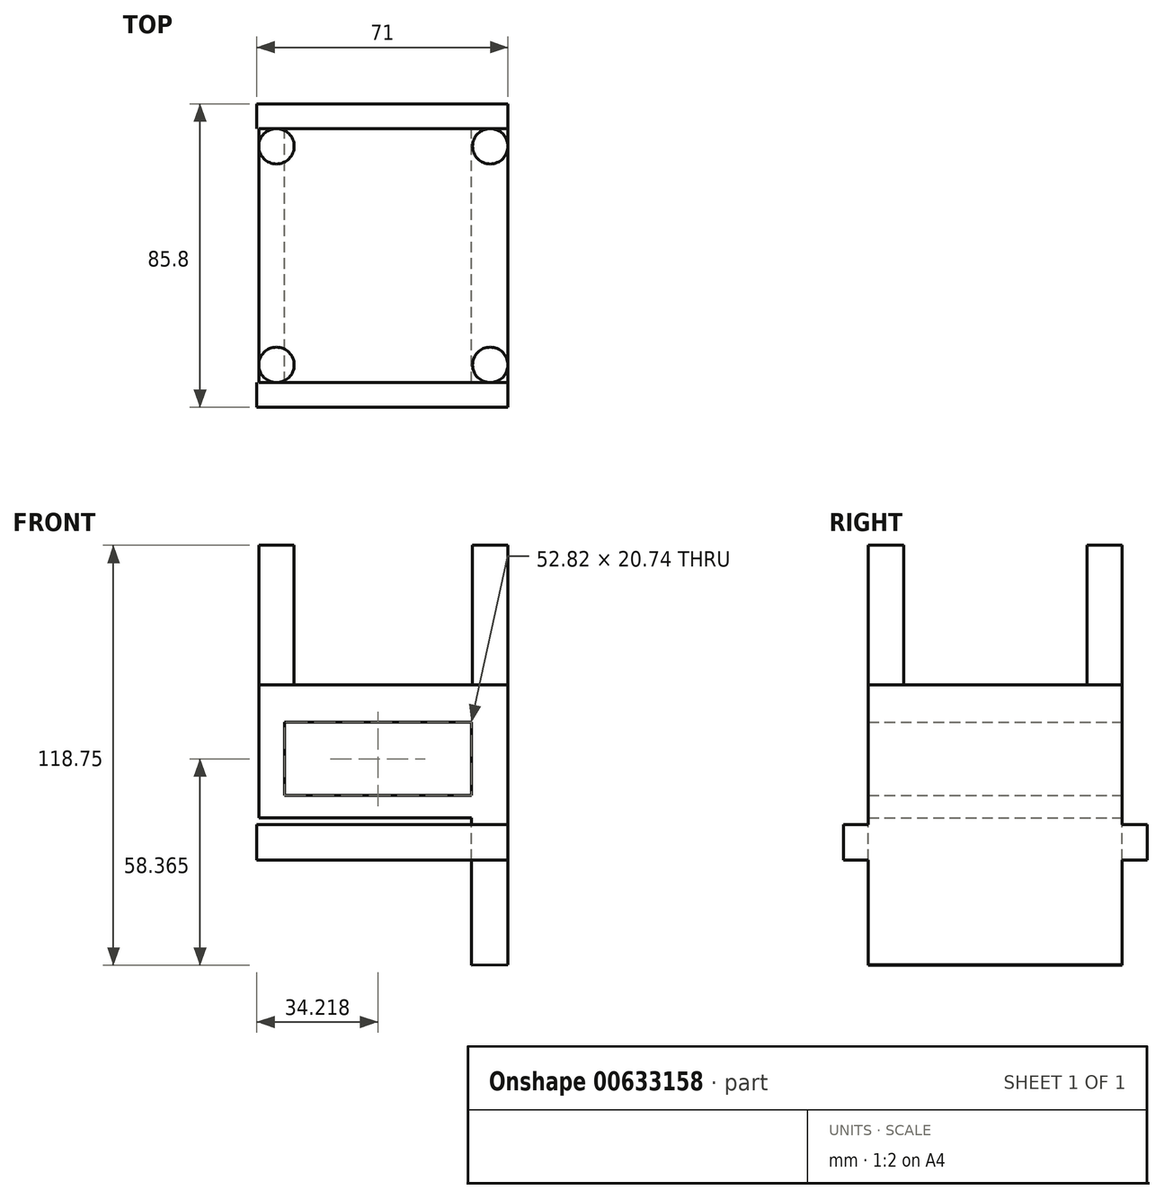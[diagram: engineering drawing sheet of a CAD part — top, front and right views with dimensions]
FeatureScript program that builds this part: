
annotation { "Feature Type Name" : "Feature", "Feature Type Description" : "" }
export const myFeature = defineFeature(function(context is Context, id is Id, definition is map)
    precondition{}
    {
        {
            var Q0;
            Q0=qCreatedBy(makeId("Front.planeOp"),FACE);
            var sketch = newSketch(context, id + "F0", { "sketchPlane" : qUnion([Q0])});
            skLineSegment(sketch, "E0", {"start": v(43.4, -44.81) * mm, "end": v(43.4, 23.93) * mm});
            skLineSegment(sketch, "E1", {"start": v(43.4, 23.93) * mm, "end": v(-16.65, 23.93) * mm});
            skLineSegment(sketch, "E2", {"start": v(-16.65, 23.93) * mm, "end": v(-16.65, 34.54) * mm});
            skLineSegment(sketch, "E3", {"start": v(-16.65, 34.54) * mm, "end": v(53.78, 34.54) * mm});
            skLineSegment(sketch, "E4", {"start": v(53.78, 34.54) * mm, "end": v(53.78, -44.57) * mm});
            skLineSegment(sketch, "E5", {"start": v(53.78, -44.57) * mm, "end": v(43.4, -44.81) * mm});
            skLineSegment(sketch, "E6", {"start": v(43.4, -3.09) * mm, "end": v(-16.65, -3.09) * mm});
            skLineSegment(sketch, "E7", {"start": v(-16.65, -3.09) * mm, "end": v(-16.65, 23.93) * mm});
            skLineSegment(sketch, "E8", {"start": v(43.4, 3.18) * mm, "end": v(-9.41, 3.18) * mm});
            skLineSegment(sketch, "E9", {"start": v(-9.41, 3.18) * mm, "end": v(-9.41, 23.93) * mm});
            skSolve(sketch);
        }
        {
            var Q0;
            Q0 = qSketchRegion(id + "F0", true);
            extrude(context, id + "F1", {"entities" : qUnion([Q0]), "depth" : 71.8 * mm, "offsetDistance" : 25 * mm});
        }
        {
            var Q0;
            Q0=makeQuery(id+"F1.opExtrude","SWEPT_FACE",FACE,{"disambiguationData":[OSD([sQuery(id+"F0.wireOp",EDGE,"E3")])]});
            var sketch = newSketch(context, id + "F2", { "sketchPlane" : qUnion([Q0])});
            skLineSegment(sketch, "E10", {"start": v(-16.65, -71.8) * mm, "end": v(-16.65, -66.8) * mm});
            skLineSegment(sketch, "E11", {"start": v(-11.65, -66.8) * mm, "end": v(-16.65, -66.8) * mm});
            skLineSegment(sketch, "E12", {"start": v(-16.65, 0) * mm, "end": v(-16.65, -5) * mm});
            skLineSegment(sketch, "E13", {"start": v(-16.65, -5) * mm, "end": v(-11.65, -5) * mm});
            skLineSegment(sketch, "E14", {"start": v(53.78, 0) * mm, "end": v(53.78, -5) * mm});
            skLineSegment(sketch, "E15", {"start": v(48.78, -5) * mm, "end": v(53.78, -5) * mm});
            skLineSegment(sketch, "E16", {"start": v(53.78, -71.8) * mm, "end": v(53.78, -66.8) * mm});
            skLineSegment(sketch, "E17", {"start": v(48.78, -66.8) * mm, "end": v(53.78, -66.8) * mm});
            skCircle(sketch, "E18", {"center": v(-11.65, -66.8) * mm, "radius": 5 * mm});
            skCircle(sketch, "E19", {"center": v(48.78, -66.8) * mm, "radius": 5 * mm});
            skCircle(sketch, "E20", {"center": v(48.78, -5) * mm, "radius": 5 * mm});
            skCircle(sketch, "E21", {"center": v(-11.65, -5) * mm, "radius": 5 * mm});
            skSolve(sketch);
        }
        {
            var Q0;
            Q0 = qSketchRegion(id + "F2", true);
            extrude(context, id + "F3", {"entities" : qUnion([Q0]), "operationType" : NewBodyOperationType.ADD, "depth" : 39.4 * mm, "offsetDistance" : 25 * mm});
        }
        {
            var Q0;
            Q0=makeQuery(id+"F1.opExtrude","CAP_FACE",FACE,{"disambiguationData":[OSD([sQuery(id+"F0.wireOp",EDGE,"E0"),sQuery(id+"F0.wireOp",EDGE,"E1"),sQuery(id+"F0.wireOp",EDGE,"E2"),sQuery(id+"F0.wireOp",EDGE,"E3"),sQuery(id+"F0.wireOp",EDGE,"E4"),sQuery(id+"F0.wireOp",EDGE,"E5"),sQuery(id+"F0.wireOp",EDGE,"E6"),sQuery(id+"F0.wireOp",EDGE,"E7"),sQuery(id+"F0.wireOp",EDGE,"E8"),sQuery(id+"F0.wireOp",EDGE,"E9")])],"isStart":false});
            var sketch = newSketch(context, id + "F4", { "sketchPlane" : qUnion([Q0])});
            skLineSegment(sketch, "E22.bottom", {"start": v(53.78, -5.02) * mm, "end": v(44.78, -5.02) * mm});
            skLineSegment(sketch, "E22.top", {"start": v(53.78, -15.02) * mm, "end": v(44.78, -15.02) * mm});
            skLineSegment(sketch, "E22.left", {"start": v(53.78, -5.02) * mm, "end": v(53.78, -15.02) * mm});
            skLineSegment(sketch, "E22.right", {"start": v(44.78, -5.02) * mm, "end": v(44.78, -15.02) * mm});
            skSolve(sketch);
        }
        {
            var Q0;
            Q0 = qSketchRegion(id + "F4", true);
            extrude(context, id + "F5", {"entities" : qUnion([Q0]), "operationType" : NewBodyOperationType.ADD, "depth" : 7 * mm, "offsetDistance" : 25 * mm});
        }
        {
            var Q0;
            Q0=makeQuery(id+"F1.opExtrude","CAP_FACE",FACE,{"disambiguationData":[OSD([sQuery(id+"F0.wireOp",EDGE,"E0"),sQuery(id+"F0.wireOp",EDGE,"E1"),sQuery(id+"F0.wireOp",EDGE,"E2"),sQuery(id+"F0.wireOp",EDGE,"E3"),sQuery(id+"F0.wireOp",EDGE,"E4"),sQuery(id+"F0.wireOp",EDGE,"E5"),sQuery(id+"F0.wireOp",EDGE,"E6"),sQuery(id+"F0.wireOp",EDGE,"E7"),sQuery(id+"F0.wireOp",EDGE,"E8"),sQuery(id+"F0.wireOp",EDGE,"E9")])],"isStart":true});
            var sketch = newSketch(context, id + "F6", { "sketchPlane" : qUnion([Q0])});
            skLineSegment(sketch, "E23.bottom", {"start": v(-53.78, -5.02) * mm, "end": v(-44.78, -5.02) * mm});
            skLineSegment(sketch, "E23.top", {"start": v(-53.78, -15.02) * mm, "end": v(-44.78, -15.02) * mm});
            skLineSegment(sketch, "E23.left", {"start": v(-53.78, -5.02) * mm, "end": v(-53.78, -15.02) * mm});
            skLineSegment(sketch, "E23.right", {"start": v(-44.78, -5.02) * mm, "end": v(-44.78, -15.02) * mm});
            skSolve(sketch);
        }
        {
            var Q0;
            Q0 = qSketchRegion(id + "F6", true);
            extrude(context, id + "F7", {"entities" : qUnion([Q0]), "operationType" : NewBodyOperationType.ADD, "depth" : 7 * mm, "offsetDistance" : 25 * mm});
        }
        {
            var Q0;
            Q0=makeQuery(id+"F5.opExtrude","SWEPT_FACE",FACE,{"disambiguationData":[OSD([sQuery(id+"F4.wireOp",EDGE,"E22.right")])]});
            extrude(context, id + "F8", {"entities" : qUnion([Q0]), "operationType" : NewBodyOperationType.ADD, "depth" : 62 * mm, "offsetDistance" : 25 * mm});
        }
        {
            var Q0;
            Q0=makeQuery(id+"F7.opExtrude","SWEPT_FACE",FACE,{"disambiguationData":[OSD([sQuery(id+"F6.wireOp",EDGE,"E23.right")])]});
            extrude(context, id + "F9", {"entities" : qUnion([Q0]), "operationType" : NewBodyOperationType.ADD, "depth" : 62 * mm, "offsetDistance" : 25 * mm});
        }
    });
